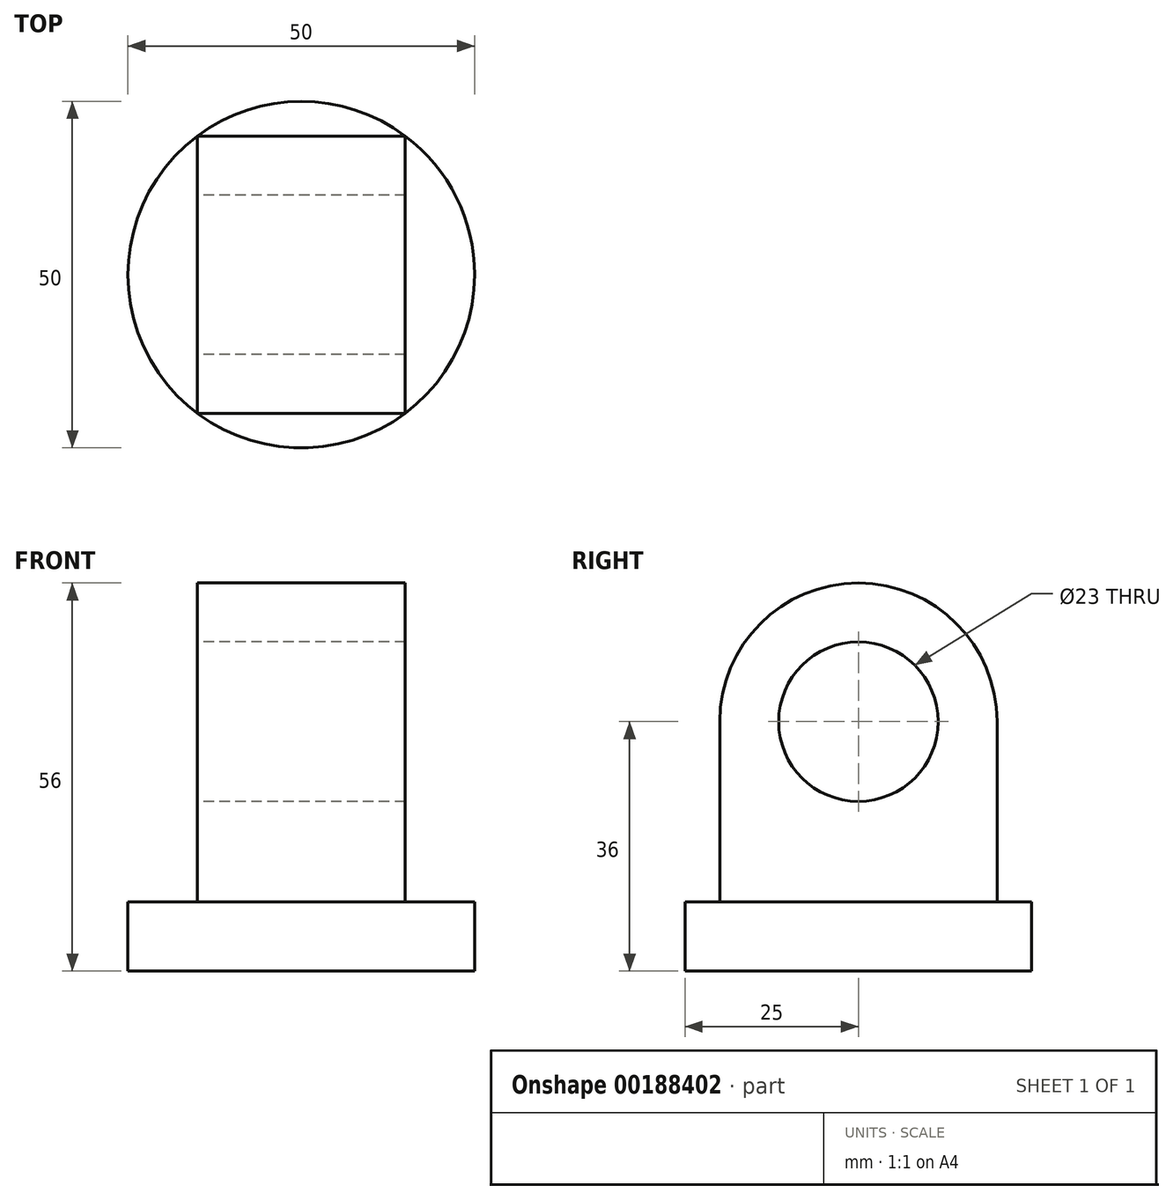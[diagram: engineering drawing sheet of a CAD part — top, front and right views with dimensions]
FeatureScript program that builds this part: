
annotation { "Feature Type Name" : "Feature", "Feature Type Description" : "" }
export const myFeature = defineFeature(function(context is Context, id is Id, definition is map)
    precondition{}
    {
        {
            var Q0;
            Q0=qCreatedBy(makeId("Top.planeOp"),FACE);
            var sketch = newSketch(context, id + "F0", { "sketchPlane" : qUnion([Q0])});
            skCircle(sketch, "E0", {"center": v(0, 0) * mm, "radius": 25 * mm});
            skSolve(sketch);
        }
        {
            var Q0;
            Q0 = qSketchRegion(id + "F0", true);
            extrude(context, id + "F1", {"entities" : qUnion([Q0]), "depth" : 10 * mm});
        }
        {
            var Q0;
            Q0=qCreatedBy(makeId("Right.planeOp"),FACE);
            var sketch = newSketch(context, id + "F2", { "sketchPlane" : qUnion([Q0])});
            skLineSegment(sketch, "E1.top", {"start": v(-20, 10) * mm, "end": v(20, 10) * mm});
            skLineSegment(sketch, "E1.left", {"start": v(-20, 36) * mm, "end": v(-20, 10) * mm});
            skLineSegment(sketch, "E1.right", {"start": v(20, 36) * mm, "end": v(20, 10) * mm});
            skArc(sketch, "E2", {"start": v(20, 36) * mm, "mid": v(0, 56) * mm, "end": v(-20, 36) * mm});
            skCircle(sketch, "E3", {"center": v(0, 36) * mm, "radius": 11.5 * mm});
            skSolve(sketch);
        }
        {
            var Q0;
            Q0 = qSketchRegion(id + "F2", true);
            extrude(context, id + "F3", {"entities" : qUnion([Q0]), "endBound" : BoundingType.SYMMETRIC, "depth" : 30 * mm});
        }
    });
